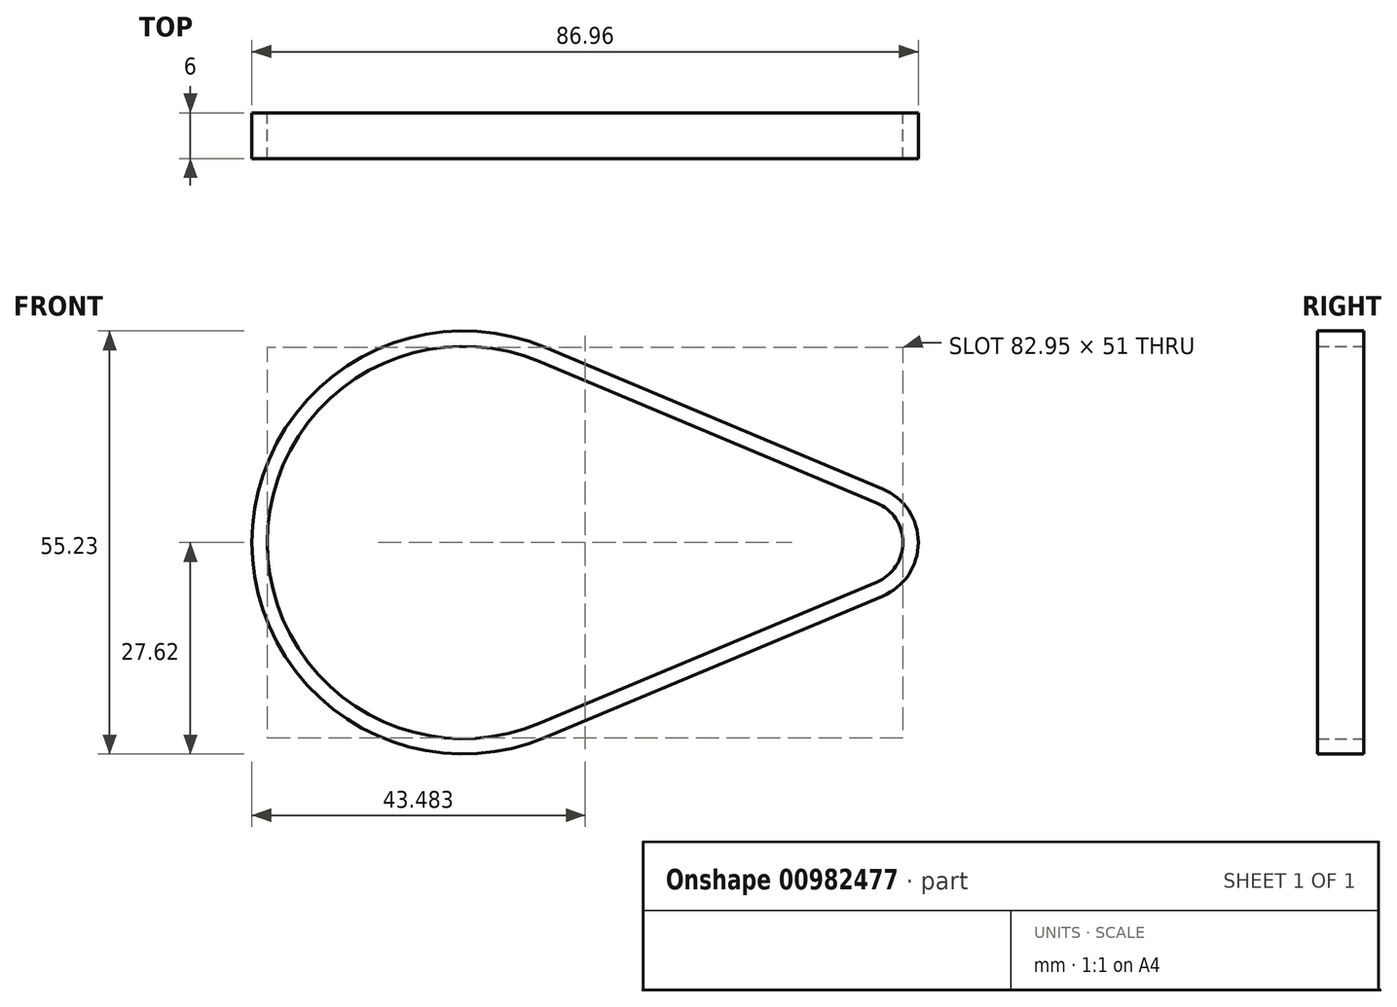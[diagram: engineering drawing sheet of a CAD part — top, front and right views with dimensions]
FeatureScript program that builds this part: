
annotation { "Feature Type Name" : "Feature", "Feature Type Description" : "" }
export const myFeature = defineFeature(function(context is Context, id is Id, definition is map)
    precondition{}
    {
        {
            var Q0;
            Q0=qCreatedBy(makeId("Front.planeOp"),FACE);
            var sketch = newSketch(context, id + "F0", { "sketchPlane" : qUnion([Q0])});
            skCircle(sketch, "E0", {"center": v(0, 0) * mm, "radius": 3 * mm});
            skLineSegment(sketch, "E1", {"start": v(0, 0) * mm, "end": v(-51.74, 0) * mm, "construction": true});
            skCircle(sketch, "E2", {"center": v(-51.74, 0) * mm, "radius": 4 * mm});
            skLineSegment(sketch, "E3", {"start": v(-41.83, 23.62) * mm, "end": v(2.17, 5.16) * mm});
            skLineSegment(sketch, "E4", {"start": v(-41.83, -23.62) * mm, "end": v(2.17, -5.16) * mm});
            skArc(sketch, "E5", {"start": v(-41.83, 23.62) * mm, "mid": v(-77.35, 0) * mm, "end": v(-41.83, -23.62) * mm});
            skArc(sketch, "E6", {"start": v(2.17, 5.16) * mm, "mid": v(5.6, 0) * mm, "end": v(2.17, -5.16) * mm});
            skLineSegment(sketch, "E7", {"start": v(2.17, 5.16) * mm, "end": v(0, 0) * mm, "construction": true});
            skLineSegment(sketch, "E8", {"start": v(2.17, -5.16) * mm, "end": v(0, 0) * mm, "construction": true});
            skArc(sketch, "E9.0", {"start": v(-41.06, 25.47) * mm, "mid": v(-79.36, 0) * mm, "end": v(-41.06, -25.47) * mm});
            skLineSegment(sketch, "E9.1", {"start": v(-41.06, 25.47) * mm, "end": v(2.94, 7) * mm});
            skArc(sketch, "E9.2", {"start": v(2.94, 7) * mm, "mid": v(7.6, 0) * mm, "end": v(2.94, -7) * mm});
            skLineSegment(sketch, "E9.3", {"start": v(-41.06, -25.47) * mm, "end": v(2.94, -7) * mm});
            skSolve(sketch);
        }
        {
            var Q0;
            Q0=qSketchRegion(id+"F0",true);
            extrude(context, id + "F1", {"entities" : qUnion([Q0]), "depth" : 6 * mm, "offsetDistance" : 25 * mm});
        }
    });
